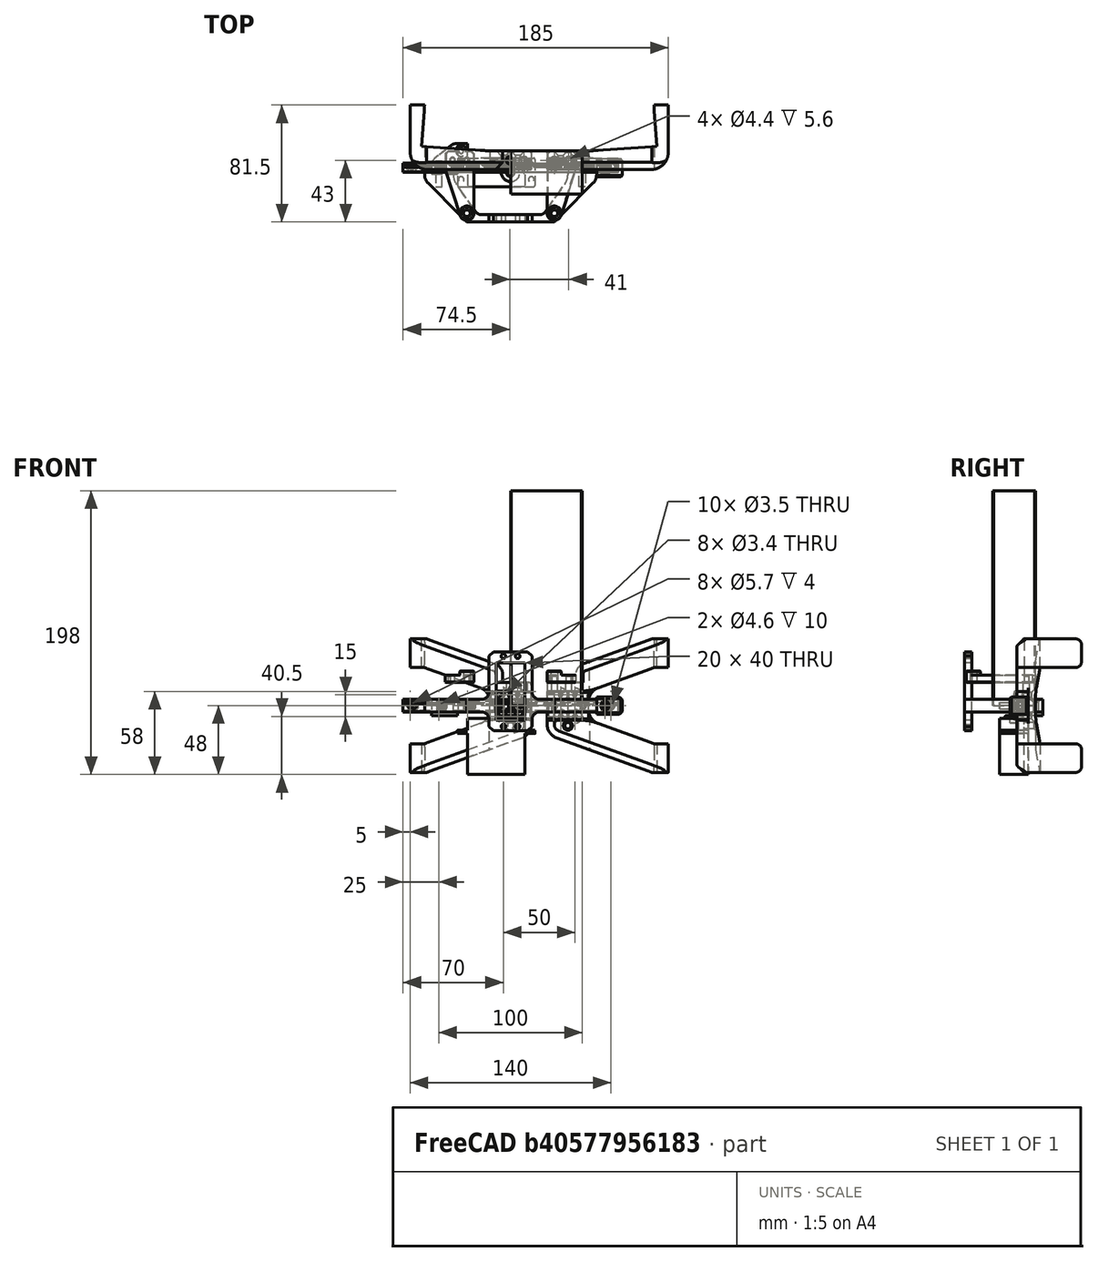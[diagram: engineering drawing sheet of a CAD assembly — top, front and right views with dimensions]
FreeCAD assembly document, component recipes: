
FREECAD ASSEMBLY — COMPONENT RECIPES ("gripper")

This assembly document has 2 components, labeled P0..P1 below (a component is one placed body or linked part). 1 of them carries a construction recipe — the FreeCAD feature program that regenerates the part from scratch, quoted from this document or its linked companion documents; the rest are supplied as boundary geometry only. No exploded tour is included for this assembly.
COMPONENT P0 — recipe-attached ("ServoPalonnier", modeled in this document).
Construction recipe (the document's own serialized feature program — sketch geometry with constraints, then the solid features built on it; lengths are millimeters unless a unit is written):

FEATURE [Sketcher::SketchObject] Sketch088
  ArcFitTolerance = 0
  ExternalBSplineMaxDegree = 0
  ExternalBSplineTolerance = 0
  FixShape = 1
  FullyConstrained = true
  InternalTolerance = 1e-06
  InvalidShape = false
  MakeInternals = false
  MapMode = 5
  TreeRank = 0
  ValidateShape = false
  sketch-geometry (7):
    g0: Circle CenterX=0 CenterY=0 CenterZ=0 NormalX=0 NormalY=0 NormalZ=1 AngleXU=0 Radius=10
    g1: Circle CenterX=0 CenterY=7 CenterZ=0 NormalX=0 NormalY=0 NormalZ=1 AngleXU=0 Radius=1.5
    g2: Circle CenterX=7 CenterY=0 CenterZ=0 NormalX=0 NormalY=0 NormalZ=1 AngleXU=0 Radius=1.5
    g3: Circle CenterX=0 CenterY=-7 CenterZ=0 NormalX=0 NormalY=0 NormalZ=1 AngleXU=0 Radius=1.5
    g4: Circle CenterX=-7 CenterY=0 CenterZ=0 NormalX=0 NormalY=0 NormalZ=1 AngleXU=0 Radius=1.5
    g5: Circle [constr] CenterX=0 CenterY=0 CenterZ=0 NormalX=0 NormalY=0 NormalZ=1 AngleXU=0 Radius=7
    g6: Circle CenterX=0 CenterY=0 CenterZ=0 NormalX=0 NormalY=0 NormalZ=1 AngleXU=0 Radius=1.5
  constraints (18):
    c: Coincident(g0,g-1)
    c: Diameter(g0) = 20
    c: PointOnObject(g1,g-2)
    c: PointOnObject(g2,g-1)
    c: PointOnObject(g3,g-2)
    c: PointOnObject(g4,g-1)
    c: Equal(g4,g1)
    c: Equal(g1,g2)
    c: Equal(g2,g3)
    c: Diameter(g1) = 3
    c: Coincident(g5,g0)
    c: PointOnObject(g1,g5)
    c: PointOnObject(g2,g5)
    c: PointOnObject(g3,g5)
    c: PointOnObject(g4,g5)
    c: DistanceX(g4,g2) = 14
    c: Coincident(g6,g0)
    c: Equal(g2,g6)
FEATURE [PartDesign::Pad] Pad052
  AddSubType = 0
  AutoTaperInnerAngle = true
  CheckUpToFaceLimits = true
  ClaimChildren = false
  Direction = (0,0,1)
  Fit = 0
  FitJoin = 0
  FixShape = 1
  InnerFit = 0
  InnerFitJoin = 0
  InvalidShape = false
  Length = 2
  Length2 = 100
  NewSolid = false
  Profile = -> Sketch088
  Refine = true
  Reversed = true
  Suppress = false
  TaperInnerAngle = 0
  TaperInnerAngleRev = 0
  TreeRank = 0
  Type = 0
  ValidateShape = true
  _ProfileBasedVersion = 0
FEATURE [Sketcher::SketchObject] Sketch089
  ArcFitTolerance = 0
  ExternalBSplineMaxDegree = 0
  ExternalBSplineTolerance = 0
  FixShape = 1
  FullyConstrained = true
  InternalTolerance = 1e-06
  InvalidShape = false
  MakeInternals = false
  MapMode = 5
  TreeRank = 0
  ValidateShape = false
  sketch-geometry (2):
    g0: Circle CenterX=0 CenterY=0 CenterZ=0 NormalX=0 NormalY=0 NormalZ=1 AngleXU=0 Radius=4.7
    g1: Circle CenterX=0 CenterY=0 CenterZ=0 NormalX=0 NormalY=0 NormalZ=1 AngleXU=0 Radius=3
  constraints (4):
    c: Coincident(g0,g-1)
    c: Coincident(g1,g0)
    c: Diameter(g0) = 9.4
    c: Diameter(g1) = 6
FEATURE [PartDesign::Pad] Pad051
  AddSubType = 0
  AutoTaperInnerAngle = true
  BaseFeature = -> Pad052
  CheckUpToFaceLimits = true
  ClaimChildren = false
  Direction = (0,0,1)
  Fit = 0
  FitJoin = 0
  FixShape = 1
  InnerFit = 0
  InnerFitJoin = 0
  InvalidShape = false
  Length = 5.4
  Length2 = 100
  NewSolid = false
  Profile = -> Sketch089
  Refine = true
  Reversed = true
  Suppress = false
  TaperInnerAngle = 0
  TaperInnerAngleRev = 0
  TreeRank = 0
  Type = 0
  ValidateShape = true
  _ProfileBasedVersion = 0
FEATURE [PartDesign::Body] Body042  label="RoundServoHorn"
  AutoGroupSolids = false
  ClaimAllChildren = false
  ExportMode = 0
  FixShape = 1
  Group = -> [Sketch088,Pad052,Sketch089,Pad051]
  InvalidShape = false
  Origin = -> Origin063
  Placement = pos=(0,0,0) rot=(1,0,0;1.5708rad)
  SingleSolid = true
  Tip = -> Pad051
  TreeRank = 211
  ValidateShape = false
  _ExportChildren = -> [Pad052,Pad051]
  _GroupVersion = 1
COMPONENT P1 — geometry summary ("GripperCaisses"; no construction recipe available for this part):
  bounding box: 220.0 x 93.1 x 80.5 mm
  tessellated surface: 75,268 triangles
  volume: 169397 mm^3 (10% of its bounding box)
PROVENANCE & LICENSES
A FreeCAD (.FCStd) document from a public repository crawl; recipes are the document's own serialized feature recipes (and, for linked parts, companion documents' recipes).
License: as declared in the source repository (recorded in the dataset sidecar).
